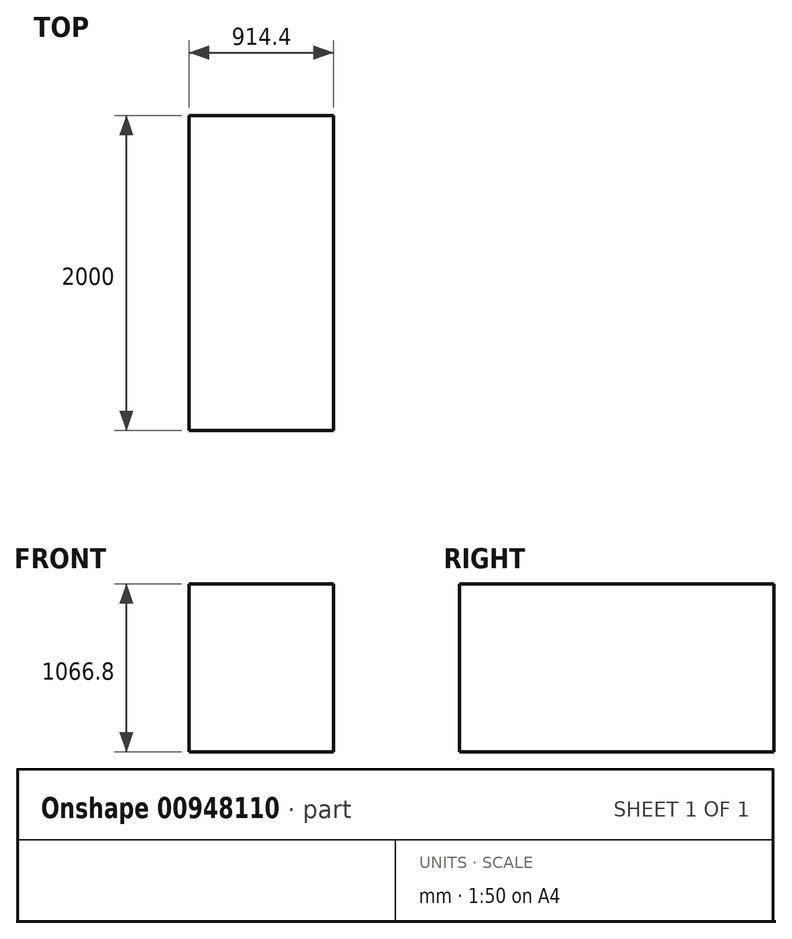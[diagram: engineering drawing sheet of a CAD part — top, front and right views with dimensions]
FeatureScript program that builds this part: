
annotation { "Feature Type Name" : "Feature", "Feature Type Description" : "" }
export const myFeature = defineFeature(function(context is Context, id is Id, definition is map)
    precondition{}
    {
        {
            var Q0;
            Q0=qCreatedBy(makeId("Front.planeOp"),FACE);
            var sketch = newSketch(context, id + "F0", { "sketchPlane" : qUnion([Q0])});
            skLineSegment(sketch, "E0.bottom", {"start": v(457.2, 533.4) * mm, "end": v(-457.2, 533.4) * mm});
            skLineSegment(sketch, "E0.top", {"start": v(457.2, -533.4) * mm, "end": v(-457.2, -533.4) * mm});
            skLineSegment(sketch, "E0.left", {"start": v(457.2, 533.4) * mm, "end": v(457.2, -533.4) * mm});
            skLineSegment(sketch, "E0.right", {"start": v(-457.2, 533.4) * mm, "end": v(-457.2, -533.4) * mm});
            skPoint(sketch, "E0.middle", {"position": v(0, 0) * mm});
            skSolve(sketch);
        }
        {
            var Q0;
            Q0=makeQuery(id+"F0.imprint","IMPRINT",FACE,{"disambiguationData":[TD([[makeQuery(id+"F0.imprint","IMPRINT",EDGE,{"derivedFrom":sQuery(id+"F0.wireOp",EDGE,"E0.bottom")}),1.0]])]});
            extrude(context, id + "F1", {"entities" : qUnion([Q0]), "oppositeDirection" : true, "depth" : 2000 * mm, "offsetDistance" : 25 * mm});
        }
    });
